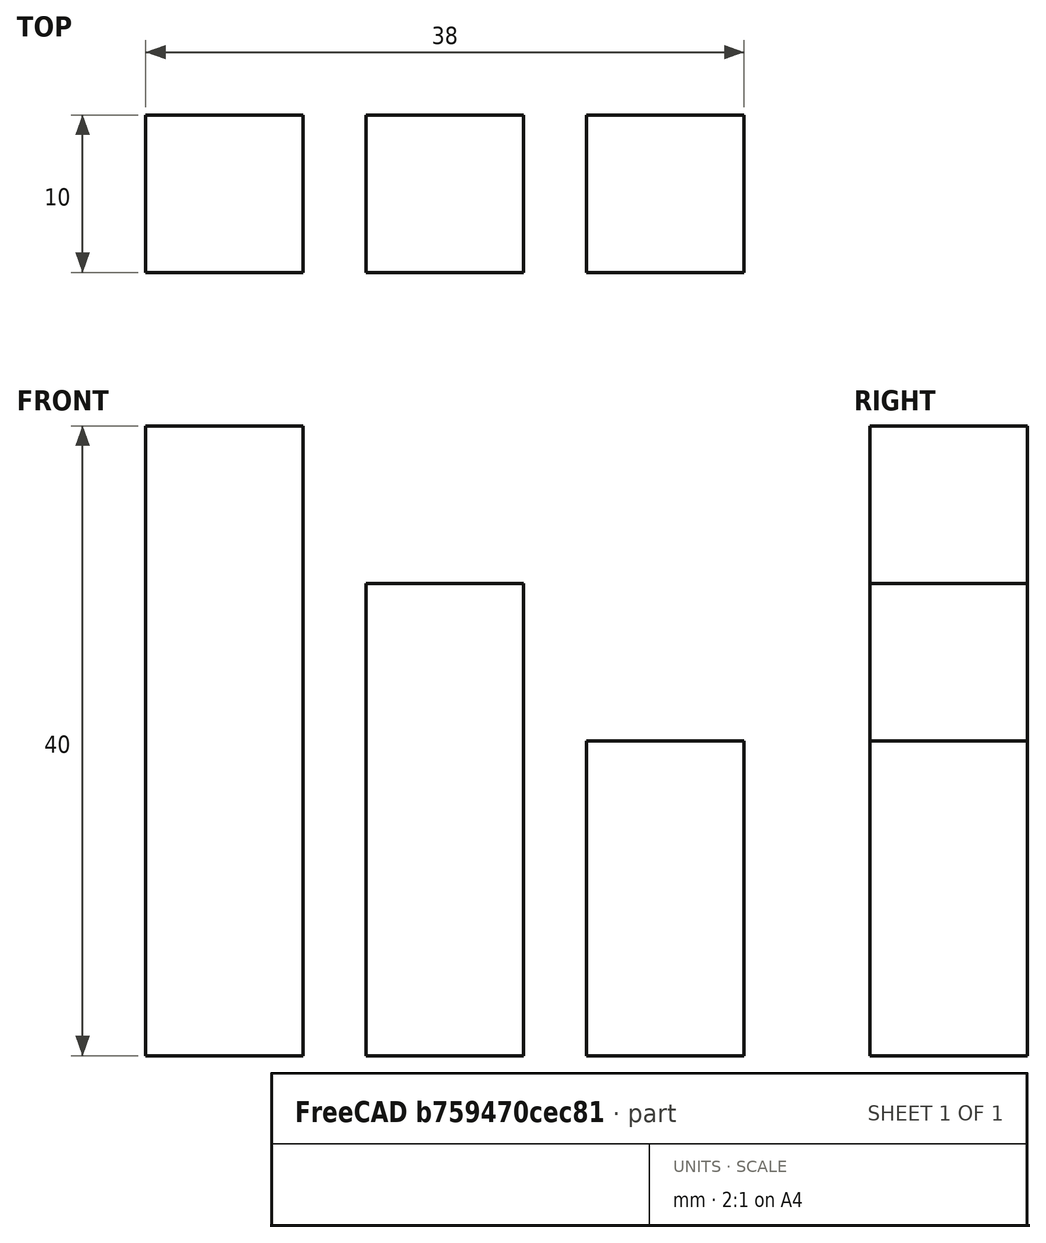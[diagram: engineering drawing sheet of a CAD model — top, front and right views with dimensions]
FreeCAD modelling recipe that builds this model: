
FCSTD DOCUMENT  (FreeCAD 0.17R13509 (Git))
Label: mode_vectors
License: All rights reserved
LicenseURL: http://en.wikipedia.org/wiki/All_rights_reserved
objects: Part::Box×9, Part::MultiFuse×3
note: 12 computed .brp shape members not serialized (recipe doc carries the construction recipe); baked Part::Feature solids carry a one-line shape summary decoded from their .brp

FEATURE [Part::Box] Box  label="Cube"
  AttacherType = Attacher::AttachEngine3D
  Height = 10
  Length = 10
  Width = 10
FEATURE [Part::Box] Box001  label="Cube001"
  AttacherType = Attacher::AttachEngine3D
  Height = 10
  Length = 10
  Placement = pos=(0,0,10) rot=(0,0,1;0rad)
  Width = 10
FEATURE [Part::Box] Box002  label="Cube002"
  AttacherType = Attacher::AttachEngine3D
  Height = 10
  Length = 10
  Placement = pos=(0,0,20) rot=(0,0,1;0rad)
  Width = 10
FEATURE [Part::Box] Box003  label="Cube003"
  AttacherType = Attacher::AttachEngine3D
  Height = 10
  Length = 10
  Placement = pos=(0,0,30) rot=(0,0,1;0rad)
  Width = 10
FEATURE [Part::MultiFuse] Fusion  label="Mode 1"
  Shapes = -> [Box,Box003,Box001,Box002]
FEATURE [Part::Box] Box004  label="Cube004"
  AttacherType = Attacher::AttachEngine3D
  Height = 10
  Length = 10
  Placement = pos=(14,0,0) rot=(0,0,1;0rad)
  Width = 10
FEATURE [Part::Box] Box005  label="Cube005"
  AttacherType = Attacher::AttachEngine3D
  Height = 10
  Length = 10
  Placement = pos=(14,0,10) rot=(0,0,1;0rad)
  Width = 10
FEATURE [Part::Box] Box006  label="Cube006"
  AttacherType = Attacher::AttachEngine3D
  Height = 10
  Length = 10
  Placement = pos=(14,0,20) rot=(0,0,1;0rad)
  Width = 10
FEATURE [Part::MultiFuse] Fusion001  label="Mode 2"
  Shapes = -> [Box004,Box006,Box005]
FEATURE [Part::Box] Box007  label="Cube007"
  AttacherType = Attacher::AttachEngine3D
  Height = 10
  Length = 10
  Placement = pos=(28,0,0) rot=(0,0,1;0rad)
  Width = 10
FEATURE [Part::Box] Box008  label="Cube008"
  AttacherType = Attacher::AttachEngine3D
  Height = 10
  Length = 10
  Placement = pos=(28,0,10) rot=(0,0,1;0rad)
  Width = 10
FEATURE [Part::MultiFuse] Fusion002  label="Mode 3"
  Shapes = -> [Box008,Box007]
